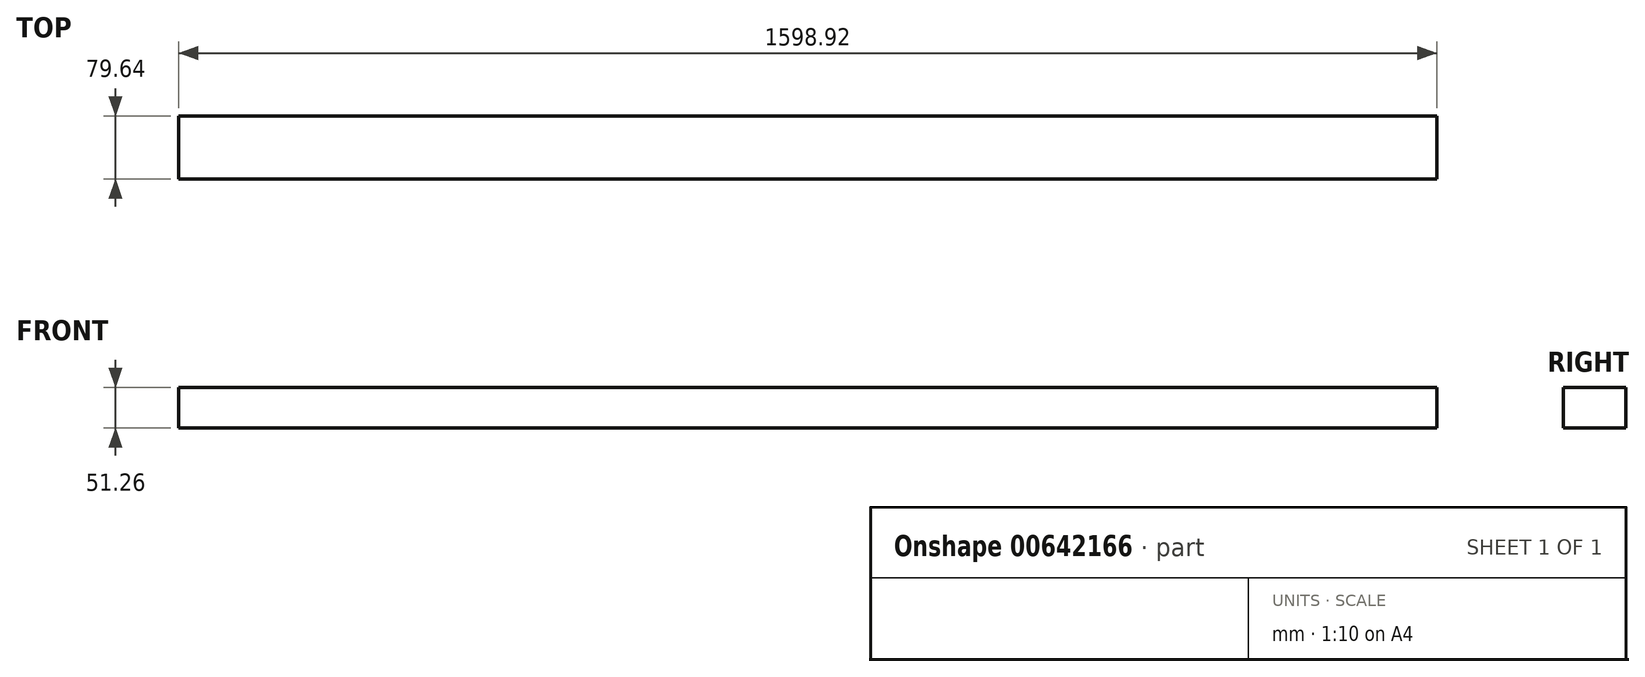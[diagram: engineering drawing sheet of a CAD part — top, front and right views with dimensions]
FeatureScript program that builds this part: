
annotation { "Feature Type Name" : "Feature", "Feature Type Description" : "" }
export const myFeature = defineFeature(function(context is Context, id is Id, definition is map)
    precondition{}
    {
        {
            var Q0;
            Q0=qCreatedBy(makeId("Front.planeOp"),FACE);
            var sketch = newSketch(context, id + "F0", { "sketchPlane" : qUnion([Q0])});
            skLineSegment(sketch, "E0.bottom", {"start": v(545.46, 51.23) * mm, "end": v(-545.46, 51.23) * mm});
            skLineSegment(sketch, "E0.top", {"start": v(545.46, -51.23) * mm, "end": v(-545.46, -51.23) * mm});
            skLineSegment(sketch, "E0.left", {"start": v(545.46, 51.23) * mm, "end": v(545.46, -51.23) * mm});
            skLineSegment(sketch, "E0.right", {"start": v(-545.46, 51.23) * mm, "end": v(-545.46, -51.23) * mm});
            skPoint(sketch, "E0.middle", {"position": v(0, 0) * mm});
            skSolve(sketch);
        }
        {
            var Q0;
            Q0=makeQuery(id+"F0.imprint","IMPRINT",FACE,{"disambiguationData":[TD([[makeQuery(id+"F0.imprint","IMPRINT",EDGE,{"derivedFrom":sQuery(id+"F0.wireOp",EDGE,"E0.bottom")}),1.0]])]});
            extrude(context, id + "F1", {"entities" : qUnion([Q0]), "depth" : 63.5 * mm, "offsetDistance" : 25.4 * mm, "hasSecondDirection" : true, "secondDirectionOppositeDirection" : true, "secondDirectionDepth" : 63.5 * mm});
        }
        {
            var Q0;
            Q0=makeQuery(id+"F1.opExtrude","SWEPT_FACE",FACE,{"disambiguationData":[OSD([sQuery(id+"F0.wireOp",EDGE,"E0.left")])]});
            var sketch = newSketch(context, id + "F2", { "sketchPlane" : qUnion([Q0])});
            skCircle(sketch, "E1", {"center": v(0, 0) * mm, "radius": 47.36 * mm});
            skSolve(sketch);
        }
        {
            var Q0;
            Q0=makeQuery(id+"F2.imprint","IMPRINT",FACE,{"disambiguationData":[TD([[makeQuery(id+"F2.imprint","IMPRINT",EDGE,{"derivedFrom":sQuery(id+"F2.wireOp",EDGE,"E1")}),-1.0]])]});
            extrude(context, id + "F3", {"entities" : qUnion([Q0]), "operationType" : NewBodyOperationType.REMOVE, "endBound" : BoundingType.THROUGH_ALL, "oppositeDirection" : true, "depth" : 25.4 * mm, "offsetDistance" : 25.4 * mm});
        }
        {
            var Q0;
            Q0=makeQuery(id+"F1.opExtrude","SWEPT_FACE",FACE,{"disambiguationData":[OSD([sQuery(id+"F0.wireOp",EDGE,"E0.left")])]});
            extrude(context, id + "F4", {"entities" : qUnion([Q0]), "operationType" : NewBodyOperationType.ADD, "depth" : 254 * mm, "offsetDistance" : 25.4 * mm});
        }
        {
            var Q0;
            Q0=makeQuery(id+"F1.opExtrude","SWEPT_FACE",FACE,{"disambiguationData":[OSD([sQuery(id+"F0.wireOp",EDGE,"E0.right")])]});
            extrude(context, id + "F5", {"entities" : qUnion([Q0]), "operationType" : NewBodyOperationType.ADD, "depth" : 254 * mm, "offsetDistance" : 25.4 * mm});
        }
        {
            var Q0;
            Q0=makeQuery(id+"F4.opExtrude","CAP_FACE",FACE,{"disambiguationData":[OSD([sQuery(id+"F0.wireOp",EDGE,"E0.left")])],"isStart":false});
            var sketch = newSketch(context, id + "F6", { "sketchPlane" : qUnion([Q0])});
            skLineSegment(sketch, "E2.bottom", {"start": v(39.82, -25.63) * mm, "end": v(-39.82, -25.63) * mm});
            skLineSegment(sketch, "E2.top", {"start": v(39.82, 25.63) * mm, "end": v(-39.82, 25.63) * mm});
            skLineSegment(sketch, "E2.left", {"start": v(39.82, -25.63) * mm, "end": v(39.82, 25.63) * mm});
            skLineSegment(sketch, "E2.right", {"start": v(-39.82, -25.63) * mm, "end": v(-39.82, 25.63) * mm});
            skPoint(sketch, "E2.middle", {"position": v(0, 0) * mm});
            skSolve(sketch);
        }
        {
            var Q0;
            {var subQ0=sQuery(id+"F6.wireOp",EDGE,"E2.left");Q0=makeQuery(id+"F6.imprint","IMPRINT",FACE,{"disambiguationData":[TD([[makeQuery(id+"F6.imprint","IMPRINT",EDGE,{"derivedFrom":subQ0}),-1.0]])]});}
            var Q1;
            {var subQ0=sQuery(id+"F6.wireOp",EDGE,"E2.right");Q1=makeQuery(id+"F6.imprint","IMPRINT",FACE,{"disambiguationData":[TD([[makeQuery(id+"F6.imprint","IMPRINT",EDGE,{"derivedFrom":subQ0}),1.0]])]});}
            var Q2;
            {var subQ0=sQuery(id+"F6.wireOp",EDGE,"E2.top");Q2=makeQuery(id+"F6.imprint","IMPRINT",FACE,{"disambiguationData":[TD([[makeQuery(id+"F6.imprint","IMPRINT",EDGE,{"derivedFrom":subQ0}),-1.0]])]});}
            var Q3;
            {var subQ0=sQuery(id+"F6.wireOp",EDGE,"E2.bottom");Q3=makeQuery(id+"F6.imprint","IMPRINT",FACE,{"disambiguationData":[TD([[makeQuery(id+"F6.imprint","IMPRINT",EDGE,{"derivedFrom":subQ0}),1.0]])]});}
            extrude(context, id + "F7", {"entities" : qUnion([Q0, Q1, Q2, Q3]), "operationType" : NewBodyOperationType.REMOVE, "endBound" : BoundingType.THROUGH_ALL, "oppositeDirection" : true, "depth" : 25.4 * mm, "offsetDistance" : 25.4 * mm});
        }
    });
